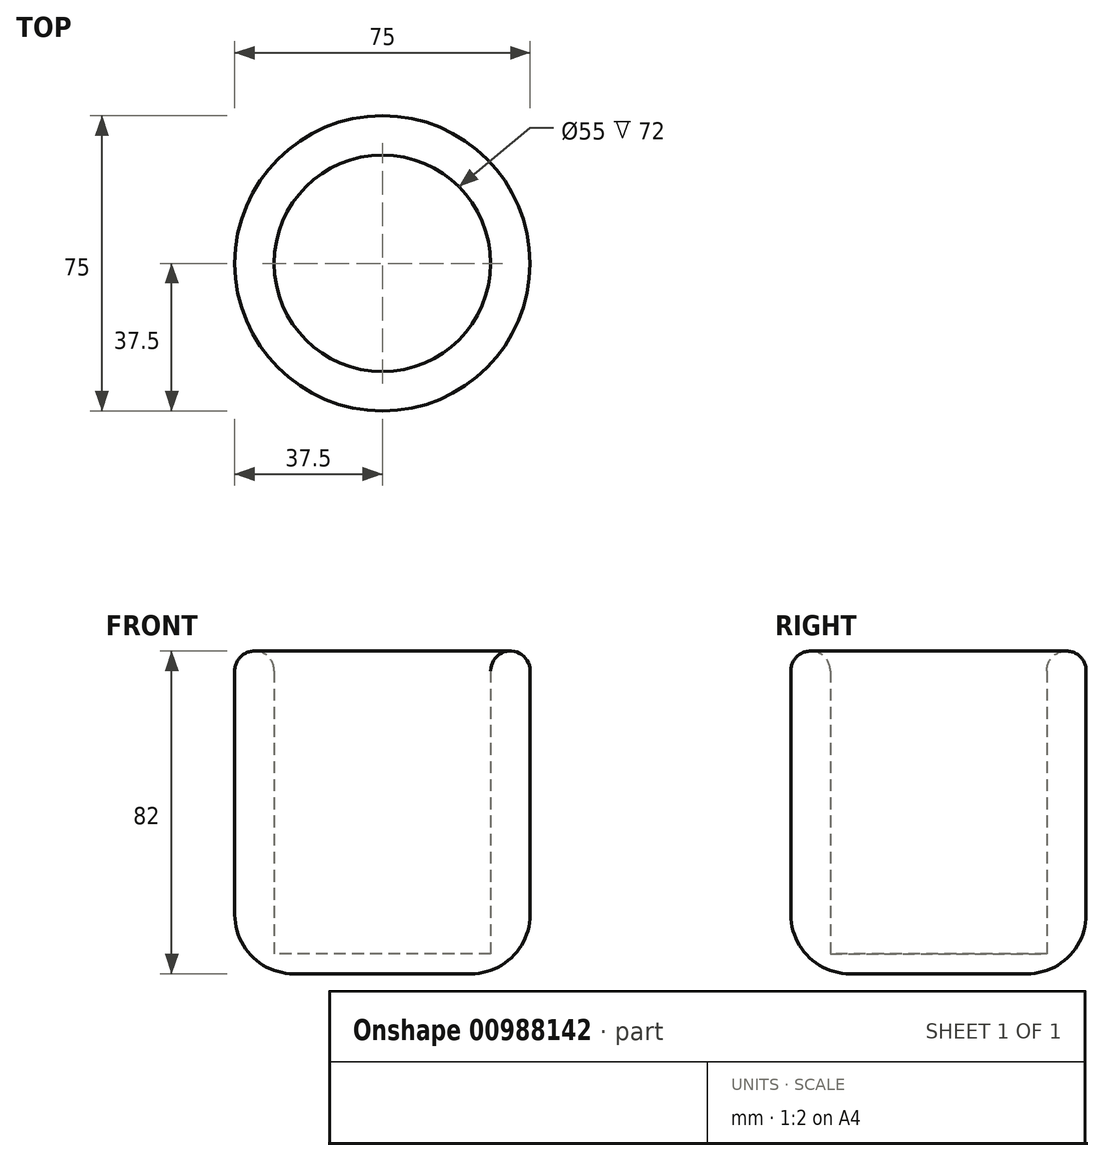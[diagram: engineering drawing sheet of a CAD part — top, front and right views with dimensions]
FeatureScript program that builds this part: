
annotation { "Feature Type Name" : "Feature", "Feature Type Description" : "" }
export const myFeature = defineFeature(function(context is Context, id is Id, definition is map)
    precondition{}
    {
        {
            var Q0;
            Q0=qCreatedBy(makeId("Top.planeOp"),FACE);
            var sketch = newSketch(context, id + "F0", { "sketchPlane" : qUnion([Q0])});
            skCircle(sketch, "E0", {"center": v(0, 0) * mm, "radius": 37.5 * mm});
            skCircle(sketch, "E1", {"center": v(0, 0) * mm, "radius": 27.5 * mm});
            skSolve(sketch);
        }
        {
            var Q0;
            Q0=makeQuery(id+"F0.imprint","IMPRINT",FACE,{"disambiguationData":[TD([[makeQuery(id+"F0.imprint","IMPRINT",EDGE,{"derivedFrom":sQuery(id+"F0.wireOp",EDGE,"E0")}),1.0]])]});
            extrude(context, id + "F1", {"entities" : qUnion([Q0]), "depth" : 82 * mm, "offsetDistance" : 25 * mm});
        }
        {
            var Q0;
            Q0=makeQuery(id+"F0.imprint","IMPRINT",FACE,{"disambiguationData":[TD([[makeQuery(id+"F0.imprint","IMPRINT",EDGE,{"derivedFrom":sQuery(id+"F0.wireOp",EDGE,"E1")}),1.0]])]});
            extrude(context, id + "F2", {"entities" : qUnion([Q0]), "operationType" : NewBodyOperationType.ADD, "depth" : 5 * mm, "offsetDistance" : 25 * mm});
        }
        {
            var Q0;
            Q0=makeQuery(id+"F1.opExtrude","CAP_EDGE",EDGE,{"disambiguationData":[OSD([sQuery(id+"F0.wireOp",EDGE,"E0")])],"isStart":true});
            fillet(context, id + "F3", {"entities" : qUnion([Q0]), "radius" : 15 * mm, "tangentPropagation" : true, "allowEdgeOverflow" : false});
        }
        {
            var Q0;
            Q0=makeQuery(id+"F1.opExtrude","CAP_EDGE",EDGE,{"disambiguationData":[OSD([sQuery(id+"F0.wireOp",EDGE,"E0")])],"isStart":false});
            fillet(context, id + "F4", {"entities" : qUnion([Q0]), "radius" : 5 * mm, "tangentPropagation" : true, "allowEdgeOverflow" : false});
        }
        {
            var Q0;
            Q0=makeQuery(id+"F1.opExtrude","CAP_EDGE",EDGE,{"disambiguationData":[OSD([sQuery(id+"F0.wireOp",EDGE,"E1")])],"isStart":false});
            fillet(context, id + "F5", {"entities" : qUnion([Q0]), "radius" : 5 * mm, "tangentPropagation" : true, "allowEdgeOverflow" : false});
        }
    });
